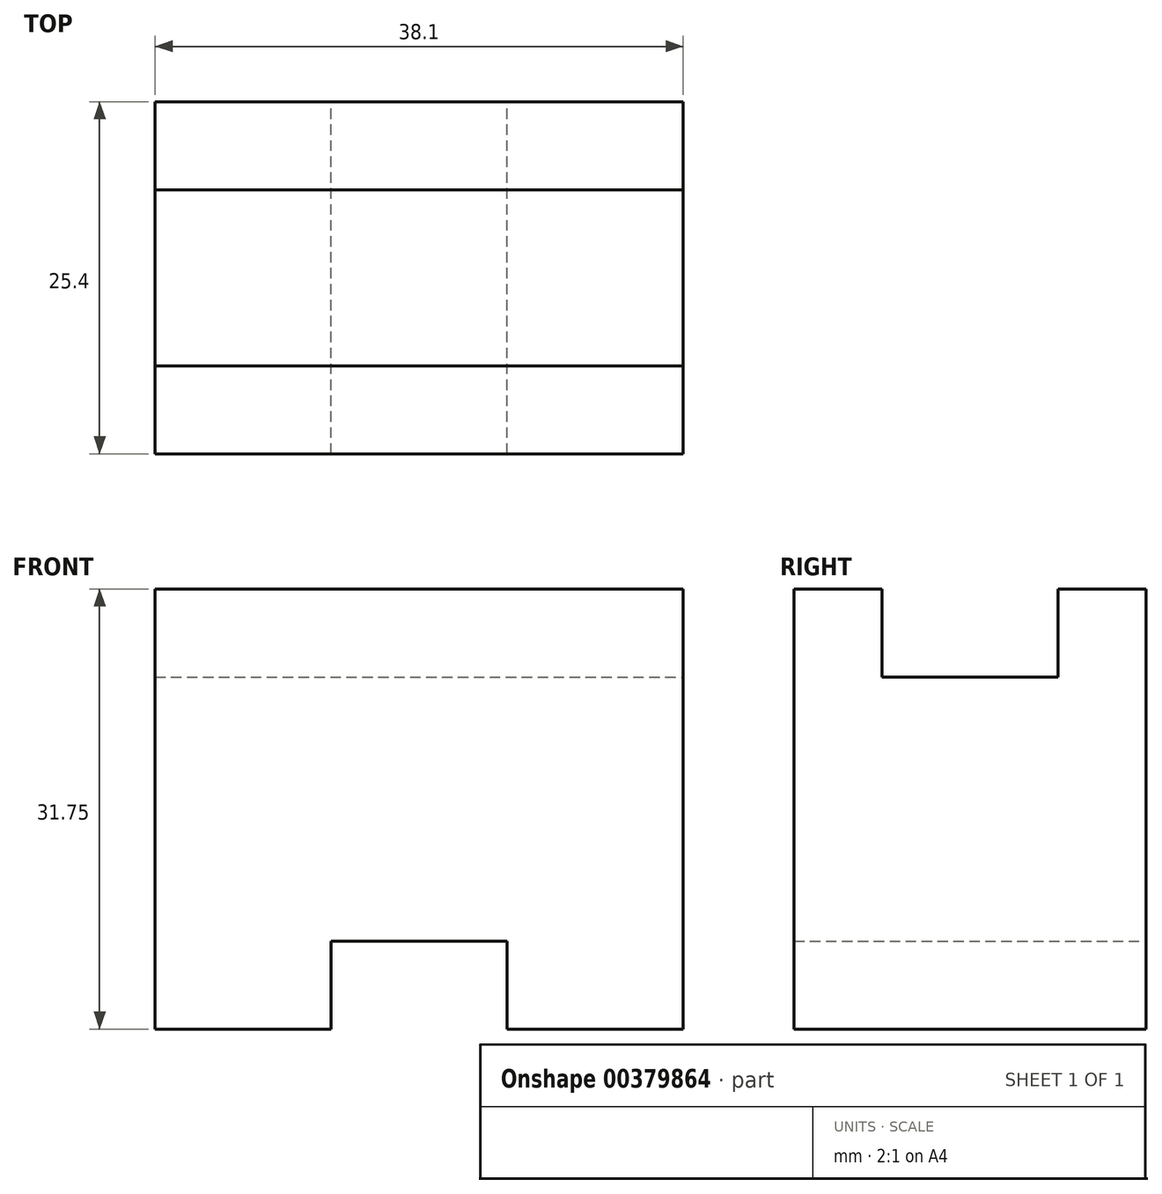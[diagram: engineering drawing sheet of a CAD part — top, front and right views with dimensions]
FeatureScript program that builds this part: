
annotation { "Feature Type Name" : "Feature", "Feature Type Description" : "" }
export const myFeature = defineFeature(function(context is Context, id is Id, definition is map)
    precondition{}
    {
        {
            var Q0;
            Q0=qCreatedBy(makeId("Front.planeOp"),FACE);
            var sketch = newSketch(context, id + "F0", { "sketchPlane" : qUnion([Q0])});
            skLineSegment(sketch, "E0", {"start": v(-50.03, 0) * mm, "end": v(-50.03, 31.75) * mm});
            skLineSegment(sketch, "E1", {"start": v(-50.03, 31.75) * mm, "end": v(-11.93, 31.75) * mm});
            skLineSegment(sketch, "E2", {"start": v(-11.93, 31.75) * mm, "end": v(-11.93, 0) * mm});
            skLineSegment(sketch, "E3", {"start": v(-50.03, 0) * mm, "end": v(-11.93, 0) * mm});
            skLineSegment(sketch, "E4", {"start": v(-50.03, 0) * mm, "end": v(-37.33, 0) * mm});
            skLineSegment(sketch, "E5", {"start": v(-11.93, 0) * mm, "end": v(-24.63, 0) * mm});
            skLineSegment(sketch, "E6", {"start": v(-24.63, 0) * mm, "end": v(-24.63, 6.35) * mm});
            skLineSegment(sketch, "E7", {"start": v(-37.33, 0) * mm, "end": v(-37.33, 6.35) * mm});
            skLineSegment(sketch, "E8", {"start": v(-37.33, 6.35) * mm, "end": v(-24.63, 6.35) * mm});
            skSolve(sketch);
        }
        {
            var Q0;
            Q0=makeQuery(id+"F0.imprint","IMPRINT",FACE,{"disambiguationData":[TD([[makeQuery(id+"F0.imprint","IMPRINT",EDGE,{"derivedFrom":sQuery(id+"F0.wireOp",EDGE,"E0")}),-1.0]])]});
            extrude(context, id + "F1", {"entities" : qUnion([Q0]), "depth" : 25.4 * mm});
        }
        {
            var Q0;
            Q0=makeQuery(id+"F1.opExtrude","SWEPT_FACE",FACE,{"disambiguationData":[OSD([sQuery(id+"F0.wireOp",EDGE,"E2")])]});
            var sketch = newSketch(context, id + "F2", { "sketchPlane" : qUnion([Q0])});
            skLineSegment(sketch, "E9", {"start": v(-25.4, 31.75) * mm, "end": v(-19.05, 31.75) * mm});
            skLineSegment(sketch, "E10", {"start": v(0, 31.75) * mm, "end": v(-6.35, 31.75) * mm});
            skLineSegment(sketch, "E11", {"start": v(-19.05, 31.75) * mm, "end": v(-19.05, 25.4) * mm});
            skLineSegment(sketch, "E12", {"start": v(-6.35, 31.75) * mm, "end": v(-6.35, 25.4) * mm});
            skLineSegment(sketch, "E13", {"start": v(-19.05, 25.4) * mm, "end": v(-6.35, 25.4) * mm});
            skSolve(sketch);
        }
        {
            var Q0;
            Q0 = qSketchRegion(id + "F2", true);
            var Q1;
            {var subQ0=sQuery(id+"F2.wireOp",EDGE,"E11");Q1=makeQuery(id+"F2.imprint","IMPRINT",FACE,{"disambiguationData":[TD([[makeQuery(id+"F2.imprint","IMPRINT",EDGE,{"derivedFrom":subQ0}),1.0]])]});}
            extrude(context, id + "F3", {"entities" : qUnion([Q0, Q1]), "operationType" : NewBodyOperationType.REMOVE, "oppositeDirection" : true, "depth" : 50.8 * mm});
        }
    });
